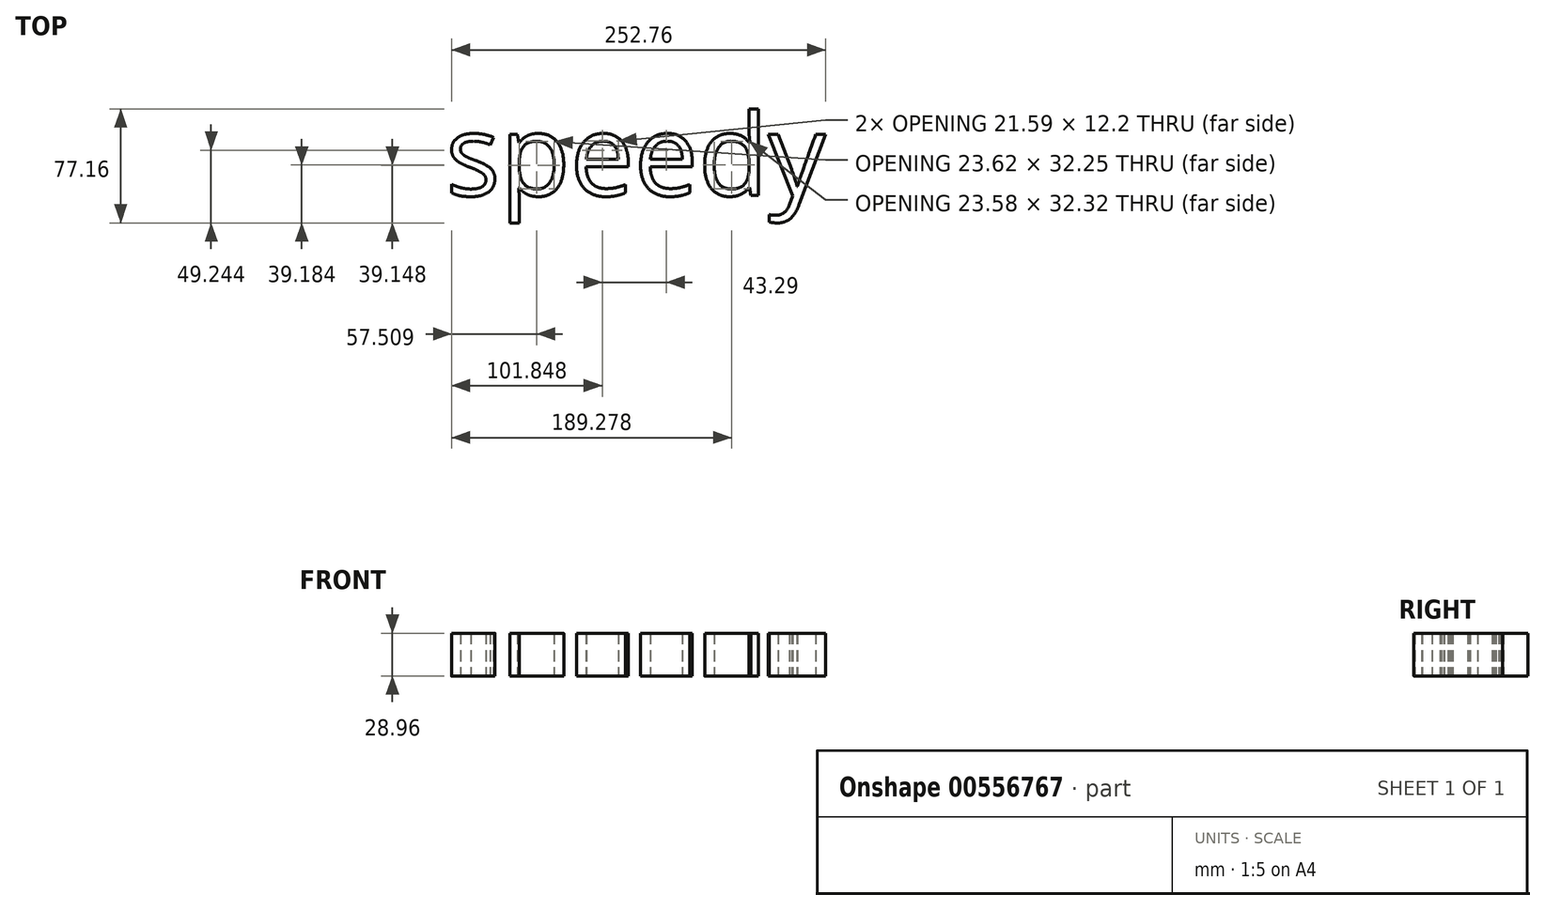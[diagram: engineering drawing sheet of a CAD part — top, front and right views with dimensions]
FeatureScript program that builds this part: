
annotation { "Feature Type Name" : "Feature", "Feature Type Description" : "" }
export const myFeature = defineFeature(function(context is Context, id is Id, definition is map)
    precondition{}
    {
        {
            var Q0;
            Q0=qCreatedBy(makeId("Top.planeOp"),FACE);
            var sketch = newSketch(context, id + "F0", { "sketchPlane" : qUnion([Q0])});
            skText(sketch, "E0", { "text": "speedy\n", "fontName": "OpenSans-Regular.ttf"});
            const initialGuessF0  = {"E0": [-0.06143, 0, 1, 0, 0.05555]};
            skSetInitialGuess(sketch, initialGuessF0);
            skSolve(sketch);
        }
        {
            var Q0;
            Q0 = qSketchRegion(id + "F0", true);
            extrude(context, id + "F1", {"entities" : qUnion([Q0]), "depth" : 28.96 * mm, "offsetDistance" : 25.4 * mm});
        }
    });
